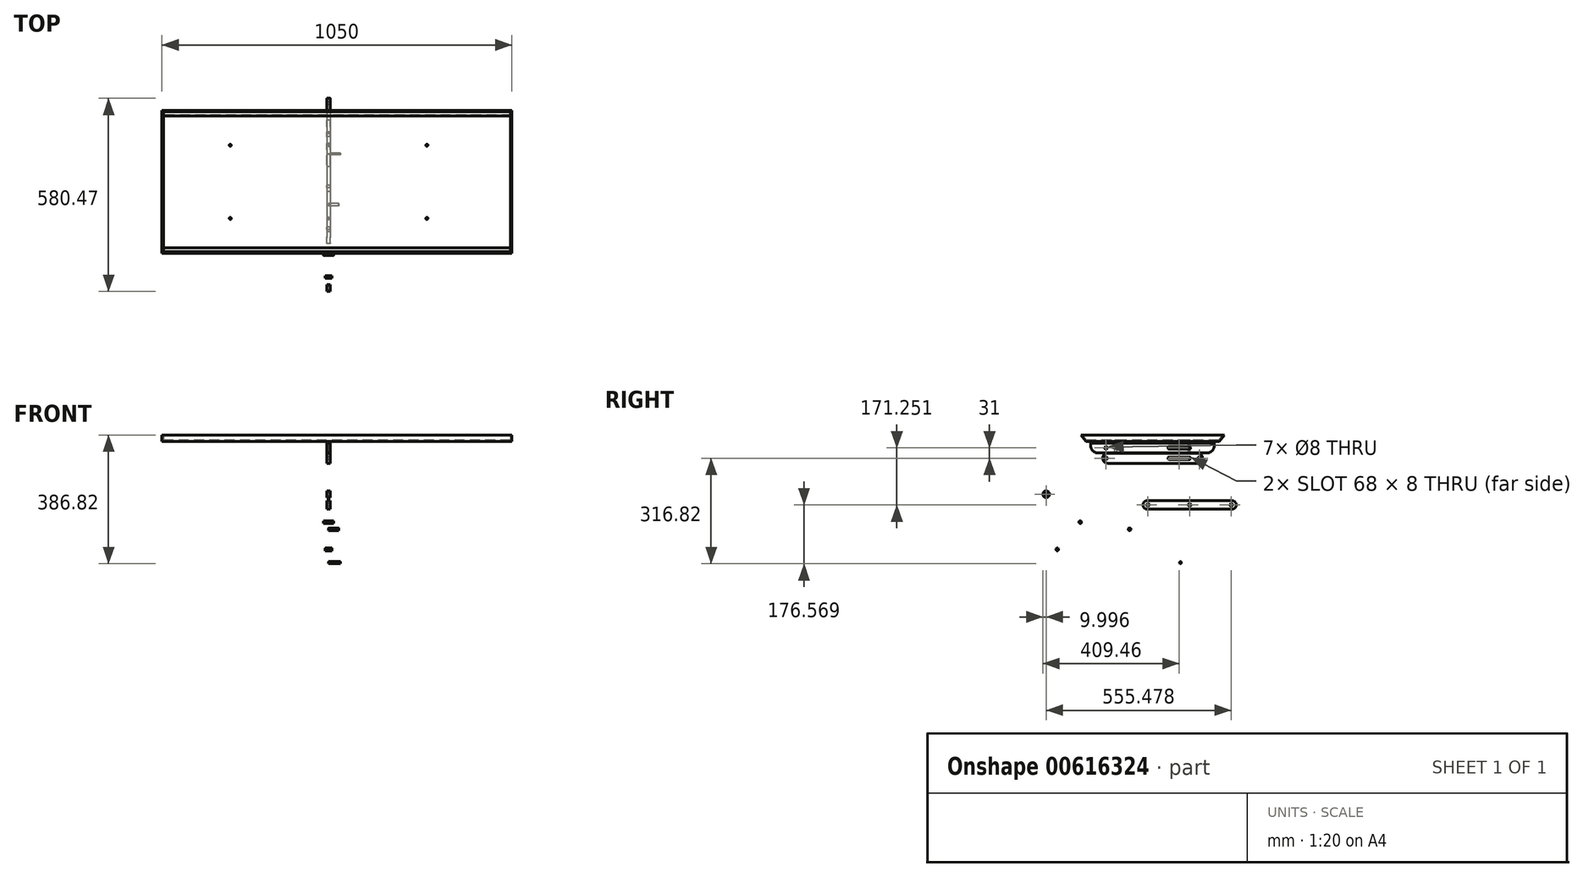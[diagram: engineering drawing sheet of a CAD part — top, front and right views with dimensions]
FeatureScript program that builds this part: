
annotation { "Feature Type Name" : "Feature", "Feature Type Description" : "" }
export const myFeature = defineFeature(function(context is Context, id is Id, definition is map)
    precondition{}
    {
        {
            var Q0;
            Q0=qCreatedBy(makeId("Right.planeOp"),FACE);
            var sketch = newSketch(context, id + "F0", { "sketchPlane" : qUnion([Q0])});
            skLineSegment(sketch, "E0.bottom", {"start": v(135, -170) * mm, "end": v(-135, -170) * mm});
            skLineSegment(sketch, "E0.top", {"start": v(135, -200) * mm, "end": v(-135, -200) * mm});
            skLineSegment(sketch, "E0.left", {"start": v(150, -185) * mm, "end": v(150, -185) * mm});
            skLineSegment(sketch, "E0.right", {"start": v(-150, -185) * mm, "end": v(-150, -185) * mm});
            skLineSegment(sketch, "E1.bottom", {"start": v(184.6, -139) * mm, "end": v(-185.4, -139) * mm});
            skLineSegment(sketch, "E1.top", {"start": v(164.6, -169) * mm, "end": v(-165.4, -169) * mm});
            skLineSegment(sketch, "E1.left", {"start": v(184.6, -139) * mm, "end": v(184.6, -149) * mm});
            skLineSegment(sketch, "E1.right", {"start": v(-185.4, -139) * mm, "end": v(-185.4, -149) * mm});
            skCircle(sketch, "E2", {"center": v(-140, -154) * mm, "radius": 4 * mm});
            skPoint(sketch, "E2.centerSnap0", {"position": v(184.6, -154) * mm});
            skPoint(sketch, "E3.centerSnap0", {"position": v(-185.4, -154) * mm});
            skCircle(sketch, "E4", {"center": v(140, -185) * mm, "radius": 4 * mm});
            skPoint(sketch, "E4.centerSnap0", {"position": v(150, -185) * mm});
            skCircle(sketch, "E5", {"center": v(-140, -185) * mm, "radius": 4 * mm});
            skPoint(sketch, "E5.centerSnap0", {"position": v(-150, -185) * mm});
            skPoint(sketch, "E6.visualSharp", {"position": v(-185.4, -169) * mm});
            skArc(sketch, "E6.filletArc", {"start": v(-185.4, -149) * mm, "mid": v(-179.55, -163.14) * mm, "end": v(-165.4, -169) * mm});
            skPoint(sketch, "E7.visualSharp", {"position": v(184.6, -169) * mm});
            skArc(sketch, "E7.filletArc", {"start": v(164.6, -169) * mm, "mid": v(178.74, -163.14) * mm, "end": v(184.6, -149) * mm});
            skPoint(sketch, "E8.visualSharp", {"position": v(150, -170) * mm});
            skArc(sketch, "E8.filletArc", {"start": v(150, -185) * mm, "mid": v(145.6, -174.4) * mm, "end": v(135, -170) * mm});
            skPoint(sketch, "E9.visualSharp", {"position": v(150, -200) * mm});
            skArc(sketch, "E9.filletArc", {"start": v(135, -200) * mm, "mid": v(145.6, -195.6) * mm, "end": v(150, -185) * mm});
            skPoint(sketch, "E10.visualSharp", {"position": v(-150, -170) * mm});
            skArc(sketch, "E10.filletArc", {"start": v(-135, -170) * mm, "mid": v(-145.6, -174.4) * mm, "end": v(-150, -185) * mm});
            skPoint(sketch, "E11.visualSharp", {"position": v(-150, -200) * mm});
            skArc(sketch, "E11.filletArc", {"start": v(-150, -185) * mm, "mid": v(-145.6, -195.6) * mm, "end": v(-135, -200) * mm});
            skLineSegment(sketch, "E12", {"start": v(50, -158) * mm, "end": v(110, -158) * mm});
            skLineSegment(sketch, "E13", {"start": v(50, -150) * mm, "end": v(110, -150) * mm});
            skLineSegment(sketch, "E14", {"start": v(110, -189) * mm, "end": v(50, -189) * mm});
            skLineSegment(sketch, "E15", {"start": v(50, -181) * mm, "end": v(110, -181) * mm});
            skCircle(sketch, "E16", {"center": v(0, 0) * mm, "radius": 245 * mm});
            skPoint(sketch, "E17.center.orphan", {"position": v(110, -185) * mm});
            skPoint(sketch, "E18.center.orphan", {"position": v(50, -185) * mm});
            skArc(sketch, "E19", {"start": v(50, -181) * mm, "mid": v(46, -185) * mm, "end": v(50, -189) * mm});
            skArc(sketch, "E20", {"start": v(110, -181) * mm, "mid": v(114, -185) * mm, "end": v(110, -189) * mm});
            skPoint(sketch, "E3.center.orphan", {"position": v(50, -154) * mm});
            skPoint(sketch, "E21.center.orphan", {"position": v(110, -154) * mm});
            skArc(sketch, "E22", {"start": v(110, -150) * mm, "mid": v(114, -154) * mm, "end": v(110, -158) * mm});
            skArc(sketch, "E23", {"start": v(50, -158) * mm, "mid": v(46, -154) * mm, "end": v(50, -150) * mm});
            skSolve(sketch);
        }
        {
            var Q0;
            Q0=makeQuery(id+"F0.imprint","IMPRINT",FACE,{"disambiguationData":[TD([[makeQuery(id+"F0.imprint","IMPRINT",EDGE,{"derivedFrom":sQuery(id+"F0.wireOp",EDGE,"E0.bottom")}),1.0]])]});
            var Q1;
            Q1=makeQuery(id+"F0.imprint","IMPRINT",FACE,{"disambiguationData":[TD([[makeQuery(id+"F0.imprint","IMPRINT",EDGE,{"derivedFrom":sQuery(id+"F0.wireOp",EDGE,"E1.bottom")}),1.0]])]});
            extrude(context, id + "F1", {"entities" : qUnion([Q0, Q1]), "endBound" : BoundingType.SYMMETRIC, "depth" : 10 * mm, "offsetDistance" : 25 * mm});
        }
        {
            var Q0;
            Q0=qCreatedBy(makeId("Right.planeOp"),FACE);
            var sketch = newSketch(context, id + "F2", { "sketchPlane" : qUnion([Q0])});
            skLineSegment(sketch, "E24.bottom", {"start": v(238.51, -312.75) * mm, "end": v(-16.49, -312.75) * mm});
            skLineSegment(sketch, "E24.top", {"start": v(238.51, -337.75) * mm, "end": v(-16.49, -337.75) * mm});
            skLineSegment(sketch, "E24.left", {"start": v(251.01, -325.25) * mm, "end": v(251.01, -325.25) * mm});
            skLineSegment(sketch, "E24.right", {"start": v(-28.99, -325.25) * mm, "end": v(-28.99, -325.25) * mm});
            skCircle(sketch, "E25", {"center": v(236.01, -325.25) * mm, "radius": 4 * mm});
            skPoint(sketch, "E25.centerSnap0", {"position": v(251.01, -325.25) * mm});
            skCircle(sketch, "E26", {"center": v(-13.99, -325.25) * mm, "radius": 4 * mm});
            skPoint(sketch, "E26.centerSnap0", {"position": v(-28.99, -325.25) * mm});
            skPoint(sketch, "E27.visualSharp", {"position": v(251.01, -312.75) * mm});
            skArc(sketch, "E27.filletArc", {"start": v(251.01, -325.25) * mm, "mid": v(247.35, -316.41) * mm, "end": v(238.51, -312.75) * mm});
            skPoint(sketch, "E28.visualSharp", {"position": v(251.01, -337.75) * mm});
            skArc(sketch, "E28.filletArc", {"start": v(238.51, -337.75) * mm, "mid": v(247.35, -334.09) * mm, "end": v(251.01, -325.25) * mm});
            skPoint(sketch, "E29.visualSharp", {"position": v(-28.99, -312.75) * mm});
            skArc(sketch, "E29.filletArc", {"start": v(-16.49, -312.75) * mm, "mid": v(-25.33, -316.41) * mm, "end": v(-28.99, -325.25) * mm});
            skPoint(sketch, "E30.visualSharp", {"position": v(-28.99, -337.75) * mm});
            skArc(sketch, "E30.filletArc", {"start": v(-28.99, -325.25) * mm, "mid": v(-25.33, -334.09) * mm, "end": v(-16.49, -337.75) * mm});
            skCircle(sketch, "E31", {"center": v(111.01, -325.25) * mm, "radius": 4 * mm});
            skPoint(sketch, "E31.centerSnap0", {"position": v(111.01, -312.75) * mm});
            skSolve(sketch);
        }
        {
            var Q0;
            Q0=makeQuery(id+"F2.imprint","IMPRINT",FACE,{"disambiguationData":[TD([[makeQuery(id+"F2.imprint","IMPRINT",EDGE,{"derivedFrom":sQuery(id+"F2.wireOp",EDGE,"E24.bottom")}),1.0]])]});
            extrude(context, id + "F3", {"entities" : qUnion([Q0]), "endBound" : BoundingType.SYMMETRIC, "depth" : 10 * mm, "offsetDistance" : 25 * mm});
        }
        {
            var Q0;
            Q0=makeQuery(id+"F0.imprint","IMPRINT",FACE,{"disambiguationData":[TD([[makeQuery(id+"F0.imprint","IMPRINT",EDGE,{"derivedFrom":sQuery(id+"F0.wireOp",EDGE,"E0.bottom")}),-1.0]])]});
            var sketch = newSketch(context, id + "F4", { "sketchPlane" : qUnion([Q0])});
            skCircle(sketch, "E32", {"center": v(-319.46, -293.22) * mm, "radius": 4 * mm});
            skCircle(sketch, "E33", {"center": v(-319.46, -293.22) * mm, "radius": 10 * mm});
            skSolve(sketch);
        }
        {
            var Q0;
            Q0=makeQuery(id+"F4.imprint","IMPRINT",FACE,{"disambiguationData":[TD([[makeQuery(id+"F4.imprint","IMPRINT",EDGE,{"derivedFrom":sQuery(id+"F4.wireOp",EDGE,"E32")}),-1.0]])]});
            extrude(context, id + "F5", {"entities" : qUnion([Q0]), "endBound" : BoundingType.SYMMETRIC, "depth" : 10 * mm, "offsetDistance" : 25 * mm});
        }
        {
            var Q0;
            Q0=makeQuery(id+"F0.imprint","IMPRINT",FACE,{"disambiguationData":[TD([[makeQuery(id+"F0.imprint","IMPRINT",EDGE,{"derivedFrom":sQuery(id+"F0.wireOp",EDGE,"E0.bottom")}),-1.0]])]});
            var sketch = newSketch(context, id + "F6", { "sketchPlane" : qUnion([Q0])});
            skCircle(sketch, "E34", {"center": v(-286.3, -459.02) * mm, "radius": 4 * mm});
            skSolve(sketch);
        }
        {
            var Q0;
            Q0=makeQuery(id+"F6.imprint","IMPRINT",FACE,{"disambiguationData":[TD([[makeQuery(id+"F6.imprint","IMPRINT",EDGE,{"derivedFrom":sQuery(id+"F6.wireOp",EDGE,"E34")}),1.0]])]});
            extrude(context, id + "F7", {"entities" : qUnion([Q0]), "endBound" : BoundingType.SYMMETRIC, "depth" : 20 * mm, "offsetDistance" : 25 * mm});
        }
        {
            var Q0;
            Q0=makeQuery(id+"F0.imprint","IMPRINT",FACE,{"disambiguationData":[TD([[makeQuery(id+"F0.imprint","IMPRINT",EDGE,{"derivedFrom":sQuery(id+"F0.wireOp",EDGE,"E0.bottom")}),-1.0]])]});
            var sketch = newSketch(context, id + "F8", { "sketchPlane" : qUnion([Q0])});
            skCircle(sketch, "E35", {"center": v(-217.26, -376.95) * mm, "radius": 4 * mm});
            skSolve(sketch);
        }
        {
            var Q0;
            Q0=makeQuery(id+"F8.imprint","IMPRINT",FACE,{"disambiguationData":[TD([[makeQuery(id+"F8.imprint","IMPRINT",EDGE,{"derivedFrom":sQuery(id+"F8.wireOp",EDGE,"E35")}),1.0]])]});
            extrude(context, id + "F9", {"entities" : qUnion([Q0]), "endBound" : BoundingType.SYMMETRIC, "depth" : 30 * mm, "offsetDistance" : 25 * mm});
        }
        {
            var Q0;
            Q0=makeQuery(id+"F0.imprint","IMPRINT",FACE,{"disambiguationData":[TD([[makeQuery(id+"F0.imprint","IMPRINT",EDGE,{"derivedFrom":sQuery(id+"F0.wireOp",EDGE,"E0.bottom")}),-1.0]])]});
            var sketch = newSketch(context, id + "F10", { "sketchPlane" : qUnion([Q0])});
            skLineSegment(sketch, "E36", {"start": v(200, -135) * mm, "end": v(-200, -135) * mm});
            skLineSegment(sketch, "E37", {"start": v(-200, -135) * mm, "end": v(-215, -115) * mm});
            skLineSegment(sketch, "E38", {"start": v(-215, -115) * mm, "end": v(215, -115) * mm});
            skLineSegment(sketch, "E39", {"start": v(215, -115) * mm, "end": v(200, -135) * mm});
            skSolve(sketch);
        }
        {
            var Q0;
            Q0=makeQuery(id+"F10.imprint","IMPRINT",FACE,{"disambiguationData":[TD([[makeQuery(id+"F10.imprint","IMPRINT",EDGE,{"derivedFrom":sQuery(id+"F10.wireOp",EDGE,"E36")}),-1.0]])]});
            extrude(context, id + "F11", {"entities" : qUnion([Q0]), "depth" : 550 * mm, "offsetDistance" : 25 * mm, "hasSecondDirection" : true, "secondDirectionOppositeDirection" : true, "secondDirectionDepth" : 500 * mm});
        }
        {
            var Q0;
            Q0=makeQuery(id+"F11.opExtrude","SWEPT_FACE",FACE,{"disambiguationData":[OSD([sQuery(id+"F10.wireOp",EDGE,"E38")])]});
            shell(context, id + "F12", {"entities" : qUnion([Q0]), "thickness" : 4 * mm});
        }
        {
            var Q0;
            Q0=makeQuery(id+"F12.opShell","OFFSET_FACE",FACE,{"disambiguationData":[OSD([sQuery(id+"F10.wireOp",EDGE,"E36")])]});
            var sketch = newSketch(context, id + "F13", { "sketchPlane" : qUnion([Q0])});
            skPoint(sketch, "E40", {"position": v(-295, -110) * mm});
            skPoint(sketch, "E41", {"position": v(-295, 110) * mm});
            skPoint(sketch, "E42.MirrorP", {"position": v(295, 110) * mm});
            skPoint(sketch, "E43.MirrorP", {"position": v(295, -110) * mm});
            skSolve(sketch);
        }
        {
            var Q0;
            Q0=sQuery(id+"F13.wireOp",VERTEX,"E41");
            var Q1;
            Q1=sQuery(id+"F13.wireOp",VERTEX,"E40");
            var Q2;
            Q2=sQuery(id+"F13.wireOp",VERTEX,"E42.MirrorP");
            var Q3;
            Q3=sQuery(id+"F13.wireOp",VERTEX,"E43.MirrorP");
            var Q4;
            Q4=makeQuery(id+"F11.opExtrude","SWEPT_BODY",BODY,{"disambiguationData":[OSD([sQuery(id+"F10.wireOp",EDGE,"E36"),sQuery(id+"F10.wireOp",EDGE,"E37"),sQuery(id+"F10.wireOp",EDGE,"E38"),sQuery(id+"F10.wireOp",EDGE,"E39")])]});
            hole(context, id + "F14", {"style" : HoleStyle.SIMPLE, "endStyle" : HoleEndStyle.THROUGH, "holeDiameter" : 6 * mm, "majorDiameter" : 5 * mm, "isTappedThrough" : true, "tappedDepth" : 12 * mm, "tapClearance" : 3, "locations" : qUnion([Q0, Q1, Q2, Q3]), "scope" : qUnion([Q4])});
        }
        {
            var Q0;
            Q0=makeQuery(id+"F1.opExtrude","SWEPT_FACE",FACE,{"disambiguationData":[OSD([sQuery(id+"F0.wireOp",EDGE,"E1.bottom")])]});
            var sketch = newSketch(context, id + "F15", { "sketchPlane" : qUnion([Q0])});
            skPoint(sketch, "E44", {"position": v(0, 110) * mm});
            skPoint(sketch, "E45", {"position": v(0, -110) * mm});
            skSolve(sketch);
        }
        {
            var Q0;
            Q0=sQuery(id+"F15.wireOp",VERTEX,"E45");
            var Q1;
            Q1=sQuery(id+"F15.wireOp",VERTEX,"E44");
            var Q2;
            Q2=makeQuery(id+"F1.opExtrude","SWEPT_BODY",BODY,{"disambiguationData":[OSD([sQuery(id+"F0.wireOp",EDGE,"E1.bottom"),sQuery(id+"F0.wireOp",EDGE,"E1.top"),sQuery(id+"F0.wireOp",EDGE,"E1.left"),sQuery(id+"F0.wireOp",EDGE,"E1.right"),sQuery(id+"F0.wireOp",EDGE,"E2"),sQuery(id+"F0.wireOp",EDGE,"E6.filletArc"),sQuery(id+"F0.wireOp",EDGE,"E7.filletArc"),sQuery(id+"F0.wireOp",EDGE,"E12"),sQuery(id+"F0.wireOp",EDGE,"E13"),sQuery(id+"F0.wireOp",EDGE,"E22"),sQuery(id+"F0.wireOp",EDGE,"E23")])]});
            hole(context, id + "F16", {"style" : HoleStyle.SIMPLE, "endStyle" : HoleEndStyle.THROUGH, "holeDiameter" : 6 * mm, "majorDiameter" : 5 * mm, "isTappedThrough" : true, "tappedDepth" : 12 * mm, "tapClearance" : 3, "locations" : qUnion([Q0, Q1]), "scope" : qUnion([Q2])});
        }
        {
            var Q0;
            Q0=makeQuery(id+"F0.imprint","IMPRINT",FACE,{"disambiguationData":[TD([[makeQuery(id+"F0.imprint","IMPRINT",EDGE,{"derivedFrom":sQuery(id+"F0.wireOp",EDGE,"E0.bottom")}),-1.0]])]});
            var sketch = newSketch(context, id + "F17", { "sketchPlane" : qUnion([Q0])});
            skCircle(sketch, "E46", {"center": v(83.47, -498.82) * mm, "radius": 3 * mm});
            skSolve(sketch);
        }
        {
            var Q0;
            Q0=makeQuery(id+"F17.imprint","IMPRINT",FACE,{"disambiguationData":[TD([[makeQuery(id+"F17.imprint","IMPRINT",EDGE,{"derivedFrom":sQuery(id+"F17.wireOp",EDGE,"E46")}),1.0]])]});
            extrude(context, id + "F18", {"entities" : qUnion([Q0]), "depth" : 35 * mm, "offsetDistance" : 25 * mm});
        }
        {
            var Q0;
            Q0=makeQuery(id+"F10.imprint","IMPRINT",FACE,{"disambiguationData":[TD([[makeQuery(id+"F10.imprint","IMPRINT",EDGE,{"derivedFrom":sQuery(id+"F10.wireOp",EDGE,"E36")}),1.0]])]});
            var sketch = newSketch(context, id + "F19", { "sketchPlane" : qUnion([Q0])});
            skCircle(sketch, "E47", {"center": v(-69.15, -398.34) * mm, "radius": 4 * mm});
            skSolve(sketch);
        }
        {
            var Q0;
            Q0=makeQuery(id+"F19.imprint","IMPRINT",FACE,{"disambiguationData":[TD([[makeQuery(id+"F19.imprint","IMPRINT",EDGE,{"derivedFrom":sQuery(id+"F19.wireOp",EDGE,"E47")}),1.0]])]});
            extrude(context, id + "F20", {"entities" : qUnion([Q0]), "depth" : 30 * mm, "offsetDistance" : 25 * mm});
        }
    });
